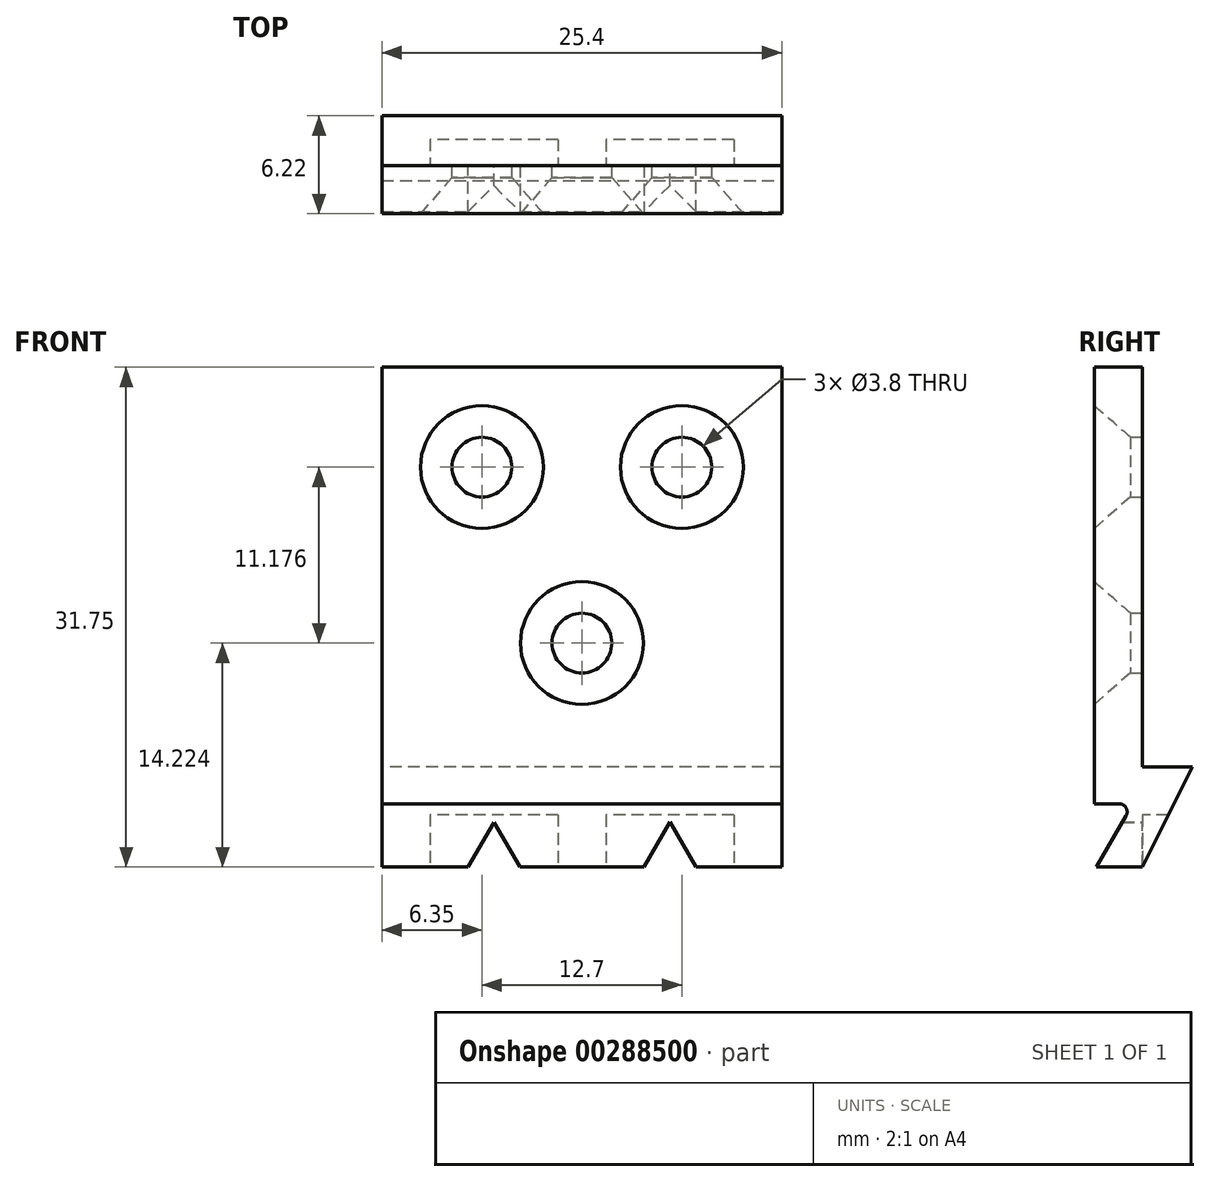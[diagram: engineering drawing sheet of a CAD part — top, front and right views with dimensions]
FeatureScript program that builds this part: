
annotation { "Feature Type Name" : "Feature", "Feature Type Description" : "" }
export const myFeature = defineFeature(function(context is Context, id is Id, definition is map)
    precondition{}
    {
        {
            var Q0;
            Q0=qCreatedBy(makeId("Right.planeOp"),FACE);
            var sketch = newSketch(context, id + "F0", { "sketchPlane" : qUnion([Q0])});
            skLineSegment(sketch, "E0", {"start": v(0, 31.75) * mm, "end": v(-3.05, 31.75) * mm});
            skLineSegment(sketch, "E1", {"start": v(-3.05, 31.75) * mm, "end": v(-3.05, 0) * mm});
            skLineSegment(sketch, "E2", {"start": v(0, 6.35) * mm, "end": v(0, 31.75) * mm});
            skLineSegment(sketch, "E3", {"start": v(-3.05, 0) * mm, "end": v(0, 0) * mm});
            skLineSegment(sketch, "E4", {"start": v(0, 0) * mm, "end": v(0, 0) * mm});
            skLineSegment(sketch, "E5", {"start": v(0, 6.35) * mm, "end": v(3.18, 6.35) * mm});
            skLineSegment(sketch, "E6", {"start": v(0, 0) * mm, "end": v(3.18, 6.35) * mm});
            skSolve(sketch);
        }
        {
            var Q0;
            Q0=makeQuery(id+"F0.imprint","IMPRINT",FACE,{"disambiguationData":[TD([[makeQuery(id+"F0.imprint","IMPRINT",EDGE,{"derivedFrom":sQuery(id+"F0.wireOp",EDGE,"E0")}),1.0]])]});
            extrude(context, id + "F1", {"entities" : qUnion([Q0]), "depth" : 25.4 * mm, "symmetric" : true});
        }
        {
            var Q0;
            Q0=makeQuery(id+"F1.opExtrude","SWEPT_FACE",FACE,{"disambiguationData":[OSD([sQuery(id+"F0.wireOp",EDGE,"E1")])]});
            var sketch = newSketch(context, id + "F2", { "sketchPlane" : qUnion([Q0])});
            skPoint(sketch, "E7", {"position": v(-6.35, 25.4) * mm});
            skPoint(sketch, "E8", {"position": v(6.35, 25.4) * mm});
            skPoint(sketch, "E9", {"position": v(0, 14.22) * mm});
            skSolve(sketch);
        }
        {
            var Q0;
            Q0=sQuery(id+"F2.wireOp",VERTEX,"E7");
            var Q1;
            Q1=sQuery(id+"F2.wireOp",VERTEX,"E8");
            var Q2;
            Q2=sQuery(id+"F2.wireOp",VERTEX,"E9");
            var Q3;
            Q3=makeQuery(id+"F1.opExtrude","SWEPT_BODY",BODY,{"disambiguationData":[OSD([sQuery(id+"F0.wireOp",EDGE,"E0"),sQuery(id+"F0.wireOp",EDGE,"E1"),sQuery(id+"F0.wireOp",EDGE,"juleGjVx-4qcC-HvIS-ZSQN-CeWkEA6BXFkq"),sQuery(id+"F0.wireOp",EDGE,"powuFhi3-pLzM-KfH9-USfb-AqJxIphrPrmo"),sQuery(id+"F0.wireOp",EDGE,"Pxiz8g5N-N8fL-KeHE-dySI-McZbkwRwocqW"),sQuery(id+"F0.wireOp",EDGE,"YuMnldA4-5GpY-13NZ-4QQo-Xug8KsLGTjK3"),sQuery(id+"F0.wireOp",EDGE,"Sq0b9Nfs-SSVs-WCv1-rVKE-iW9kM5wSggyQ"),sQuery(id+"F0.wireOp",EDGE,"E2")])]});
            hole(context, id + "F3", {"style" : HoleStyle.C_SINK, "endStyle" : HoleEndStyle.THROUGH, "standardTappedOrClearance" : lookupTablePath({ "standard" : "ANSI", "fit" : "Normal (ASME)", "size" : "#6", "type" : "Clearance" }), "standardBlindInLast" : lookupTablePath({ "fit" : "Free", "standard" : "ANSI", "size" : "#6", "type" : "Clearance" }), "holeDiameter" : 3.8 * mm, "cSinkDiameter" : 7.8 * mm, "cSinkAngle" : 82 * degree, "tappedDepth" : 12.7 * mm, "tapClearance" : 3, "locations" : qUnion([Q0, Q1, Q2]), "scope" : qUnion([Q3]), "startStyle" : HoleStartStyle.PART});
        }
        {
            var Q0;
            Q0=makeQuery(id+"F1.opExtrude","SWEPT_FACE",FACE,{"disambiguationData":[OSD([sQuery(id+"F0.wireOp",EDGE,"E2")])]});
            var sketch = newSketch(context, id + "F4", { "sketchPlane" : qUnion([Q0])});
            skLineSegment(sketch, "E10.bottom", {"start": v(-9.65, 3.3) * mm, "end": v(-1.52, 3.3) * mm});
            skLineSegment(sketch, "E10.top", {"start": v(-9.65, -6.34) * mm, "end": v(-1.52, -6.34) * mm});
            skLineSegment(sketch, "E10.left", {"start": v(-9.65, 3.3) * mm, "end": v(-9.65, -6.34) * mm});
            skLineSegment(sketch, "E10.right", {"start": v(-1.52, 3.3) * mm, "end": v(-1.52, -6.34) * mm});
            skLineSegment(sketch, "E11.bottom", {"start": v(1.52, 3.31) * mm, "end": v(9.65, 3.31) * mm});
            skLineSegment(sketch, "E11.top", {"start": v(1.52, -6.34) * mm, "end": v(9.65, -6.34) * mm});
            skLineSegment(sketch, "E11.left", {"start": v(1.52, 3.31) * mm, "end": v(1.52, -6.34) * mm});
            skLineSegment(sketch, "E11.right", {"start": v(9.65, 3.31) * mm, "end": v(9.65, -6.34) * mm});
            skSolve(sketch);
        }
        {
            var Q0;
            Q0 = qSketchRegion(id + "F4", true);
            extrude(context, id + "F5", {"entities" : qUnion([Q0]), "operationType" : NewBodyOperationType.REMOVE, "depth" : 25.4 * mm});
        }
        {
            var Q0;
            Q0=qCreatedBy(makeId("Right.planeOp"),FACE);
            var sketch = newSketch(context, id + "F6", { "sketchPlane" : qUnion([Q0])});
            skLineSegment(sketch, "E12", {"start": v(-4.45, 4.01) * mm, "end": v(-1.47, 4.01) * mm});
            skLineSegment(sketch, "E13", {"start": v(-1.03, 3.25) * mm, "end": v(-2.93, 0) * mm});
            skLineSegment(sketch, "E14", {"start": v(-2.93, 0) * mm, "end": v(-4.45, 0) * mm});
            skLineSegment(sketch, "E15", {"start": v(-4.45, 0) * mm, "end": v(-4.45, 4.01) * mm});
            skPoint(sketch, "E16.visualSharp", {"position": v(-0.58, 4.01) * mm});
            skArc(sketch, "E16.filletArc", {"start": v(-1.03, 3.25) * mm, "mid": v(-1.03, 3.76) * mm, "end": v(-1.47, 4.01) * mm});
            skSolve(sketch);
        }
        {
            var Q0;
            Q0 = qSketchRegion(id + "F6", true);
            extrude(context, id + "F7", {"entities" : qUnion([Q0]), "operationType" : NewBodyOperationType.REMOVE, "oppositeDirection" : true, "depth" : 25.4 * mm, "symmetric" : true});
        }
        {
            var Q0;
            Q0=qCreatedBy(makeId("Front.planeOp"),FACE);
            var sketch = newSketch(context, id + "F8", { "sketchPlane" : qUnion([Q0])});
            skLineSegment(sketch, "E17", {"start": v(5.59, 0) * mm, "end": v(5.59, 2.85) * mm, "construction": true});
            skCircle(sketch, "E18.cCircle", {"center": v(5.59, -3.5) * mm, "radius": 3.18 * mm, "construction": true});
            skPoint(sketch, "E18.cCircle.perimeterSnap0", {"position": v(5.59, 1.43) * mm});
            skLineSegment(sketch, "E18.0", {"start": v(11.09, -6.67) * mm, "end": v(0.09, -6.67) * mm});
            skLineSegment(sketch, "E18.1", {"start": v(0.09, -6.67) * mm, "end": v(5.59, 2.85) * mm});
            skLineSegment(sketch, "E18.2", {"start": v(5.59, 2.85) * mm, "end": v(11.09, -6.67) * mm});
            skPoint(sketch, "E18.0.midPoint", {"position": v(5.59, -6.67) * mm});
            skPoint(sketch, "E18.0.midPoint.positionSnap0", {"position": v(5.59, 1.43) * mm});
            skSolve(sketch);
        }
        {
            var Q0;
            Q0=makeQuery(id+"F8.imprint","IMPRINT",FACE,{"disambiguationData":[TD([[makeQuery(id+"F8.imprint","IMPRINT",EDGE,{"derivedFrom":sQuery(id+"F8.wireOp",EDGE,"E18.0")}),-1.0]])]});
            extrude(context, id + "F9", {"entities" : qUnion([Q0]), "operationType" : NewBodyOperationType.REMOVE, "depth" : 25.4 * mm});
        }
        {
            var Q0;
            Q0=makeQuery(id+"F5.boolean.opBoolean","COPY",FACE,{"derivedFrom":makeQuery(id+"F5.opExtrude","CAP_FACE",FACE,{"disambiguationData":[OSD([sQuery(id+"F4.wireOp",EDGE,"E11.bottom"),sQuery(id+"F4.wireOp",EDGE,"E11.top"),sQuery(id+"F4.wireOp",EDGE,"E11.left"),sQuery(id+"F4.wireOp",EDGE,"E11.right")])],"isStart":true})});
            var sketch = newSketch(context, id + "F10", { "sketchPlane" : qUnion([Q0])});
            skLineSegment(sketch, "E19", {"start": v(5.59, 0) * mm, "end": v(5.59, 3.31) * mm, "construction": true});
            skCircle(sketch, "E20.cCircle", {"center": v(5.59, -3.5) * mm, "radius": 3.18 * mm, "construction": true});
            skLineSegment(sketch, "E20.0", {"start": v(11.09, -6.68) * mm, "end": v(0.09, -6.68) * mm});
            skLineSegment(sketch, "E20.1", {"start": v(0.09, -6.68) * mm, "end": v(5.59, 2.84) * mm});
            skLineSegment(sketch, "E20.2", {"start": v(5.59, 2.84) * mm, "end": v(11.09, -6.68) * mm});
            skPoint(sketch, "E20.0.midPoint", {"position": v(5.59, -6.68) * mm});
            skSolve(sketch);
        }
        {
            var Q0;
            Q0 = qSketchRegion(id + "F10", true);
            extrude(context, id + "F11", {"entities" : qUnion([Q0]), "operationType" : NewBodyOperationType.REMOVE, "oppositeDirection" : true, "depth" : 25.4 * mm});
        }
    });
